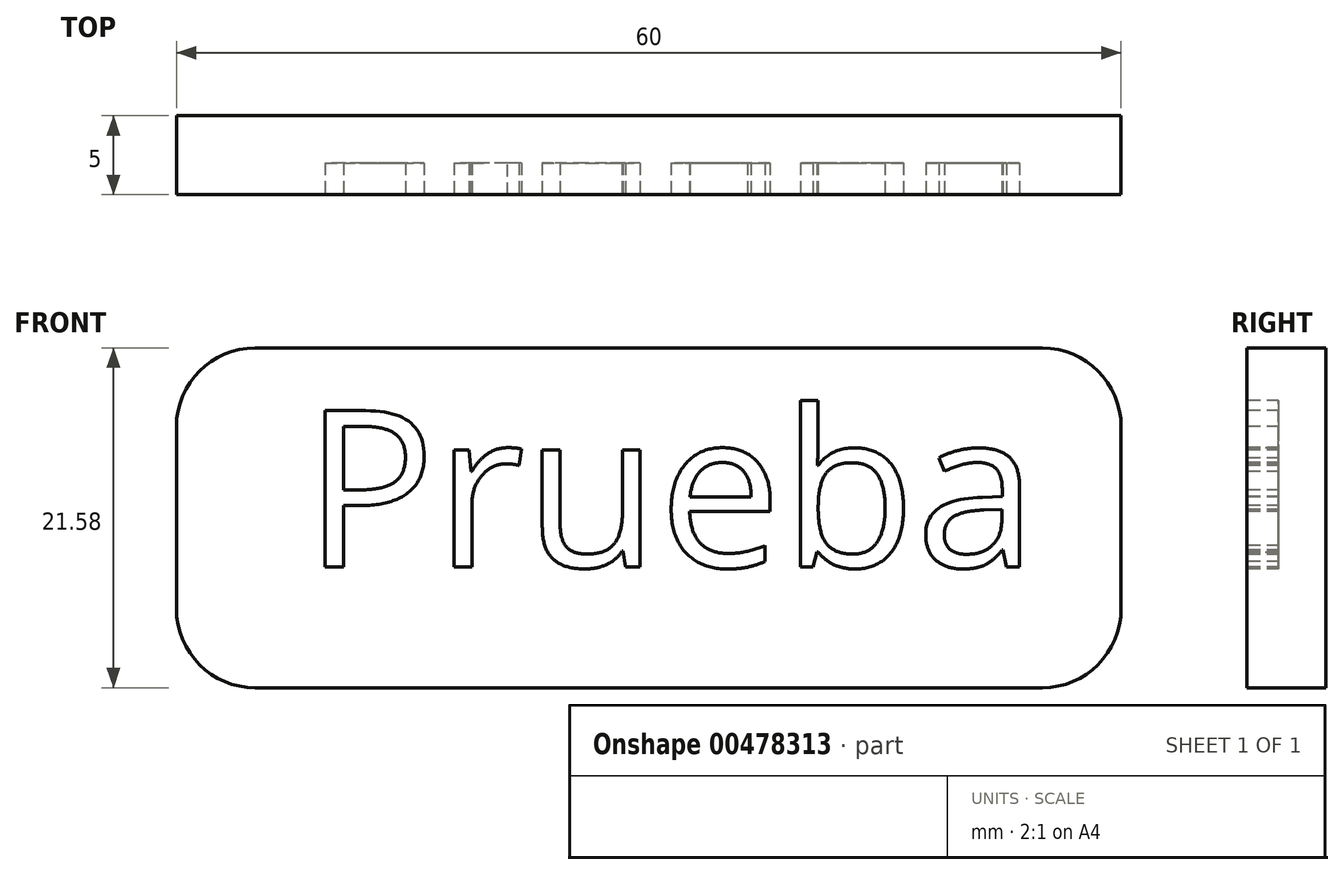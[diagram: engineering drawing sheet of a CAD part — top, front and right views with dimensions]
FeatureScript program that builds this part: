
annotation { "Feature Type Name" : "Feature", "Feature Type Description" : "" }
export const myFeature = defineFeature(function(context is Context, id is Id, definition is map)
    precondition{}
    {
        {
            var Q0;
            Q0=qCreatedBy(makeId("Front.planeOp"),FACE);
            var sketch = newSketch(context, id + "F0", { "sketchPlane" : qUnion([Q0])});
            skLineSegment(sketch, "E0.bottom", {"start": v(-31.53, -3.33) * mm, "end": v(28.47, -3.33) * mm});
            skLineSegment(sketch, "E0.top", {"start": v(-31.53, 18.25) * mm, "end": v(28.47, 18.25) * mm});
            skLineSegment(sketch, "E0.left", {"start": v(-31.53, -3.33) * mm, "end": v(-31.53, 18.25) * mm});
            skLineSegment(sketch, "E0.right", {"start": v(28.47, -3.33) * mm, "end": v(28.47, 18.25) * mm});
            skSolve(sketch);
        }
        {
            var Q0;
            Q0 = qSketchRegion(id + "F0", true);
            extrude(context, id + "F1", {"entities" : qUnion([Q0]), "depth" : 5 * mm});
        }
        {
            var Q0;
            Q0=makeQuery(id+"F1.opExtrude","CAP_FACE",FACE,{"disambiguationData":[OSD([sQuery(id+"F0.wireOp",EDGE,"E0.bottom"),sQuery(id+"F0.wireOp",EDGE,"E0.top"),sQuery(id+"F0.wireOp",EDGE,"E0.left"),sQuery(id+"F0.wireOp",EDGE,"E0.right")])],"isStart":false});
            var sketch = newSketch(context, id + "F2", { "sketchPlane" : qUnion([Q0])});
            skText(sketch, "E1", { "text": "Prueba", "fontName": "OpenSans-Regular.ttf"});
            const initialGuessF2  = {"E1": [-0.02344, 0.00435, 1, 0, 0.01]};
            skSetInitialGuess(sketch, initialGuessF2);
            skSolve(sketch);
        }
        {
            var Q0;
            Q0 = qSketchRegion(id + "F2", true);
            extrude(context, id + "F3", {"entities" : qUnion([Q0]), "operationType" : NewBodyOperationType.REMOVE, "oppositeDirection" : true, "depth" : 2 * mm});
        }
        {
            var Q0;
            Q0=makeQuery(id+"F1.opExtrude","SWEPT_EDGE",EDGE,{"disambiguationData":[OSD([sQuery(id+"F0.wireOp",EDGE,"E0.top"),sQuery(id+"F0.wireOp",EDGE,"E0.right")])]});
            var Q1;
            Q1=makeQuery(id+"F1.opExtrude","SWEPT_EDGE",EDGE,{"disambiguationData":[OSD([sQuery(id+"F0.wireOp",EDGE,"E0.bottom"),sQuery(id+"F0.wireOp",EDGE,"E0.right")])]});
            var Q2;
            Q2=makeQuery(id+"F1.opExtrude","SWEPT_EDGE",EDGE,{"disambiguationData":[OSD([sQuery(id+"F0.wireOp",EDGE,"E0.top"),sQuery(id+"F0.wireOp",EDGE,"E0.left")])]});
            var Q3;
            Q3=makeQuery(id+"F1.opExtrude","SWEPT_EDGE",EDGE,{"disambiguationData":[OSD([sQuery(id+"F0.wireOp",EDGE,"E0.bottom"),sQuery(id+"F0.wireOp",EDGE,"E0.left")])]});
            fillet(context, id + "F4", {"entities" : qUnion([Q0, Q1, Q2, Q3]), "radius" : 5 * mm, "tangentPropagation" : true, "allowEdgeOverflow" : false});
        }
    });
